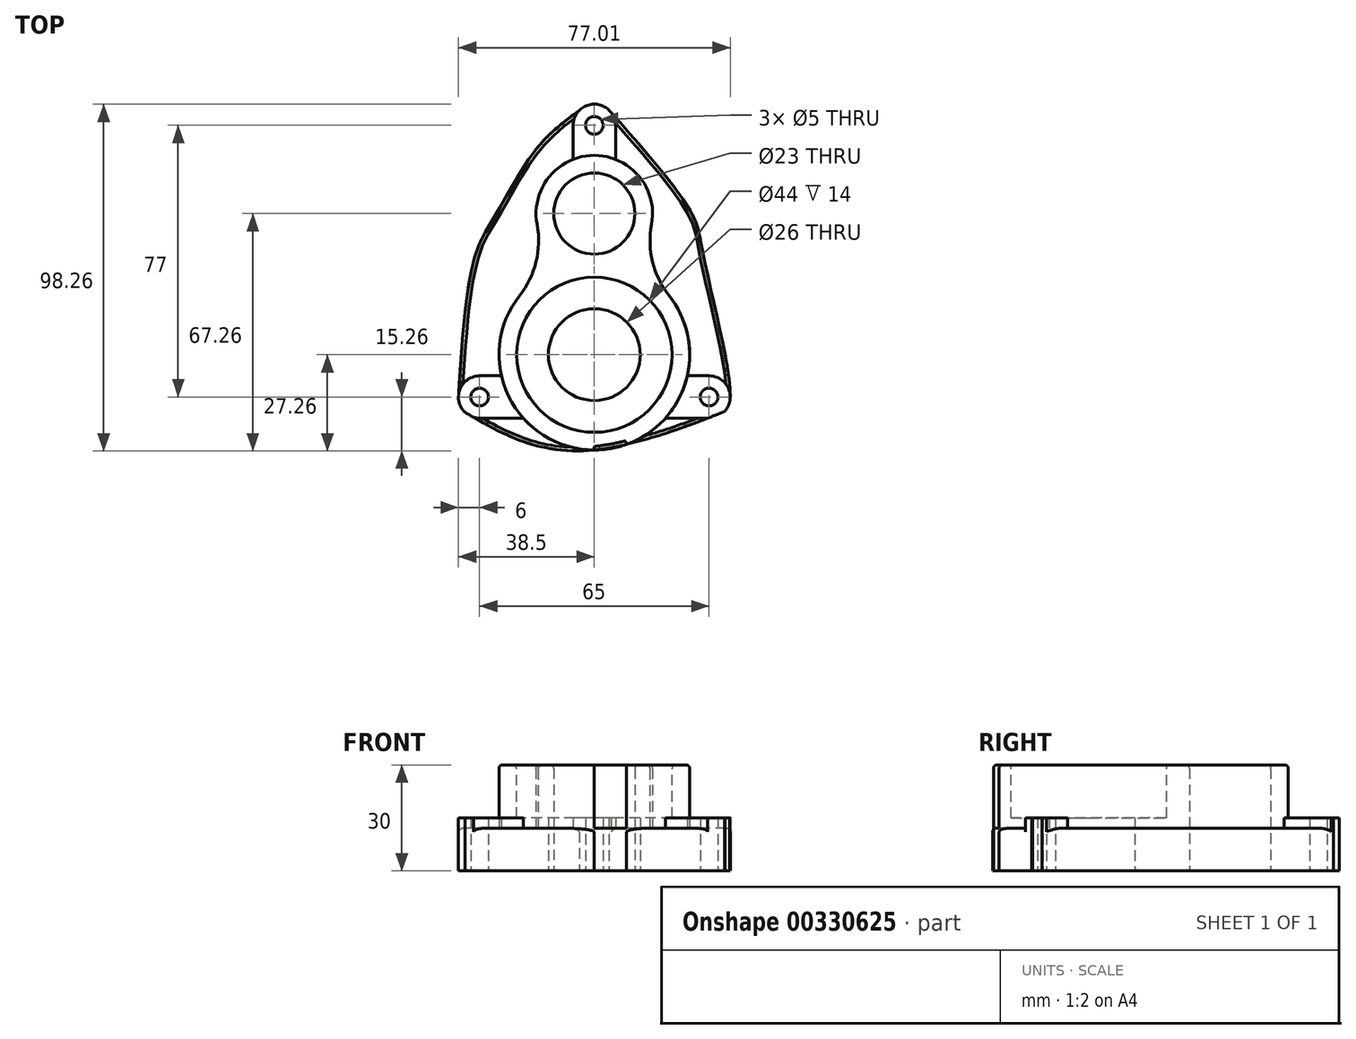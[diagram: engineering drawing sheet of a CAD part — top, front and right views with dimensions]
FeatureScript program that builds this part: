
annotation { "Feature Type Name" : "Feature", "Feature Type Description" : "" }
export const myFeature = defineFeature(function(context is Context, id is Id, definition is map)
    precondition{}
    {
        {
            var Q0;
            Q0=qCreatedBy(makeId("Top.planeOp"),FACE);
            var sketch = newSketch(context, id + "F0", { "sketchPlane" : qUnion([Q0])});
            skCircle(sketch, "E0", {"center": v(0, 0) * mm, "radius": 13 * mm});
            skCircle(sketch, "E1", {"center": v(0, 0) * mm, "radius": 22 * mm});
            skArc(sketch, "E2", {"start": v(-8.25, 25.7) * mm, "mid": v(0, -27) * mm, "end": v(8.25, 25.7) * mm});
            skCircle(sketch, "E3", {"center": v(0, 40) * mm, "radius": 11.5 * mm});
            skLineSegment(sketch, "E4", {"start": v(-46.76, -12) * mm, "end": v(88.65, -12) * mm, "construction": true});
            skLineSegment(sketch, "E5", {"start": v(85.5, 28) * mm, "end": v(-54.8, 28) * mm, "construction": true});
            skLineSegment(sketch, "E6", {"start": v(32.5, -12) * mm, "end": v(32.5, -43.46) * mm, "construction": true});
            skLineSegment(sketch, "E7", {"start": v(-32.5, -12) * mm, "end": v(-32.5, -42.32) * mm, "construction": true});
            skLineSegment(sketch, "E8", {"start": v(32.5, -43.46) * mm, "end": v(0, -43.46) * mm, "construction": true});
            skArc(sketch, "E9.0", {"start": v(8.25, 25.7) * mm, "mid": v(0, 56.5) * mm, "end": v(-8.25, 25.7) * mm});
            skCircle(sketch, "E10", {"center": v(32.5, -12) * mm, "radius": 2.5 * mm});
            skCircle(sketch, "E11", {"center": v(-32.5, -12) * mm, "radius": 2.5 * mm});
            skCircle(sketch, "E12", {"center": v(-32.5, -12) * mm, "radius": 6 * mm});
            skCircle(sketch, "E13", {"center": v(32.5, -12) * mm, "radius": 6 * mm});
            skCircle(sketch, "E14", {"center": v(0, 65) * mm, "radius": 2.5 * mm});
            skCircle(sketch, "E15", {"center": v(0, 65) * mm, "radius": 6 * mm});
            skLineSegment(sketch, "E16", {"start": v(-32.5, -6) * mm, "end": v(-26.32, -6) * mm});
            skLineSegment(sketch, "E17", {"start": v(32.5, -6) * mm, "end": v(26.32, -6) * mm});
            skLineSegment(sketch, "E18", {"start": v(32.5, -18) * mm, "end": v(20.12, -18) * mm});
            skLineSegment(sketch, "E19", {"start": v(-32.5, -18) * mm, "end": v(-20.12, -18) * mm});
            skCircle(sketch, "E20", {"center": v(-8.25, 25.7) * mm, "radius": 15 * mm, "construction": true});
            skCircle(sketch, "E21", {"center": v(8.25, 25.7) * mm, "radius": 15 * mm, "construction": true});
            skLineSegment(sketch, "E22", {"start": v(-6, 65) * mm, "end": v(-6, 55.37) * mm});
            skLineSegment(sketch, "E23", {"start": v(6, 65) * mm, "end": v(6, 55.37) * mm});
            skFitSpline(sketch, "E24", {"points": [v(-36.65, -16.33) * mm, v(0, -27) * mm, v(36.86, -16.12) * mm, v(36.84, -16.14) * mm], "startDerivative": vector(63.7, -37.15) * mm, "endDerivative": vector(-2.99, -0.84) * mm});
            skFitSpline(sketch, "E25", {"points": [v(4.21, 69.27) * mm, v(27.48, 40.3) * mm, v(30.92, 28) * mm, v(38.5, -12) * mm, v(36.86, -16.12) * mm], "startDerivative": vector(87.45, -99.48) * mm, "endDerivative": vector(-19.86, -21.82) * mm});
            skFitSpline(sketch, "E26", {"points": [v(-4.21, 69.27) * mm, v(-16.57, 58.14) * mm, v(-27.53, 40.3) * mm, v(-33.76, 28) * mm, v(-38.5, -12) * mm], "startDerivative": vector(-59.02, -43.93) * mm, "endDerivative": vector(-9.05, -137.75) * mm});
            skSolve(sketch);
        }
        {
            var Q0;
            Q0=makeQuery(id+"F0.imprint","IMPRINT",FACE,{"disambiguationData":[TD([[makeQuery(id+"F0.imprint","IMPRINT",EDGE,{"derivedFrom":sQuery(id+"F0.wireOp",EDGE,"E1")}),-1.0]])]});
            var Q1;
            {var subQ0=sQuery(id+"F0.wireOp",EDGE,"VYSbUuIq-hLQq-Rlsc-0hrW-dSPiEJNZsaO6");Q1=makeQuery(id+"F0.imprint","IMPRINT",FACE,{"disambiguationData":[TD([[makeQuery(id+"F0.imprint","IMPRINT",EDGE,{"derivedFrom":subQ0}),-1.0]])]});}
            var Q2;
            Q2=makeQuery(id+"F0.imprint","IMPRINT",FACE,{"disambiguationData":[TD([[makeQuery(id+"F0.imprint","IMPRINT",EDGE,{"derivedFrom":sQuery(id+"F0.wireOp",EDGE,"E0")}),-1.0]])]});
            var Q3;
            Q3=makeQuery(id+"F0.imprint","IMPRINT",FACE,{"disambiguationData":[TD([[makeQuery(id+"F0.imprint","IMPRINT",EDGE,{"derivedFrom":sQuery(id+"F0.wireOp",EDGE,"E0")}),1.0]])]});
            extrude(context, id + "F1", {"entities" : qUnion([Q0, Q1, Q2, Q3]), "depth" : 30 * mm});
        }
        {
            var Q0;
            {var subQ0=sQuery(id+"F0.wireOp",EDGE,"E9.0");var subQ1=sQuery(id+"F0.wireOp",EDGE,"E2");Q0=makeQuery(id+"F1.opExtrude","SWEPT_EDGE",EDGE,{"disambiguationData":[OSD([subQ1,subQ0]),TDD([makeQuery(id+"F0.imprint","INTERSECT",VERTEX,{"disambiguationData":[OD(1.0)],"derivedFrom":[subQ1,subQ0]})])]});}
            var Q1;
            {var subQ0=sQuery(id+"F0.wireOp",EDGE,"E9.0");var subQ1=sQuery(id+"F0.wireOp",EDGE,"E2");Q1=makeQuery(id+"F1.opExtrude","SWEPT_EDGE",EDGE,{"disambiguationData":[OSD([subQ1,subQ0]),TDD([makeQuery(id+"F0.imprint","INTERSECT",VERTEX,{"disambiguationData":[OD(0.0)],"derivedFrom":[subQ1,subQ0]})])]});}
            fillet(context, id + "F2", {"entities" : qUnion([Q0, Q1]), "radius" : 25 * mm, "tangentPropagation" : true, "allowEdgeOverflow" : false});
        }
        {
            var Q0;
            {var subQ0=sQuery(id+"F0.wireOp",EDGE,"E22");Q0=makeQuery(id+"F0.imprint","IMPRINT",FACE,{"disambiguationData":[TD([[makeQuery(id+"F0.imprint","IMPRINT",EDGE,{"derivedFrom":subQ0}),1.0]])]});}
            var Q1;
            Q1=makeQuery(id+"F0.imprint","IMPRINT",FACE,{"disambiguationData":[TD([[makeQuery(id+"F0.imprint","IMPRINT",EDGE,{"derivedFrom":sQuery(id+"F0.wireOp",EDGE,"E14")}),-1.0]])]});
            var Q2;
            {var subQ5=sQuery(id+"F0.wireOp",EDGE,"E17");Q2=makeQuery(id+"F0.imprint","IMPRINT",FACE,{"disambiguationData":[TD([[makeQuery(id+"F0.imprint","IMPRINT",EDGE,{"derivedFrom":subQ5}),1.0]])]});}
            var Q3;
            Q3=makeQuery(id+"F0.imprint","IMPRINT",FACE,{"disambiguationData":[TD([[makeQuery(id+"F0.imprint","IMPRINT",EDGE,{"derivedFrom":sQuery(id+"F0.wireOp",EDGE,"E10")}),-1.0]])]});
            var Q4;
            {var subQ0=sQuery(id+"F0.wireOp",EDGE,"E16");Q4=makeQuery(id+"F0.imprint","IMPRINT",FACE,{"disambiguationData":[TD([[makeQuery(id+"F0.imprint","IMPRINT",EDGE,{"derivedFrom":subQ0}),-1.0]])]});}
            var Q5;
            Q5=makeQuery(id+"F0.imprint","IMPRINT",FACE,{"disambiguationData":[TD([[makeQuery(id+"F0.imprint","IMPRINT",EDGE,{"derivedFrom":sQuery(id+"F0.wireOp",EDGE,"E11")}),-1.0]])]});
            extrude(context, id + "F3", {"entities" : qUnion([Q0, Q1, Q2, Q3, Q4, Q5]), "operationType" : NewBodyOperationType.ADD, "depth" : 15 * mm});
        }
        {
            var Q0;
            {var subQ6=sQuery(id+"F0.wireOp",EDGE,"E16");Q0=makeQuery(id+"F0.imprint","IMPRINT",FACE,{"disambiguationData":[TD([[makeQuery(id+"F0.imprint","IMPRINT",EDGE,{"derivedFrom":subQ6}),1.0]])]});}
            var Q1;
            {var subQ0=sQuery(id+"F0.wireOp",EDGE,"E17");Q1=makeQuery(id+"F0.imprint","IMPRINT",FACE,{"disambiguationData":[TD([[makeQuery(id+"F0.imprint","IMPRINT",EDGE,{"derivedFrom":subQ0}),-1.0]])]});}
            var Q2;
            {var subQ0=sQuery(id+"F0.wireOp",EDGE,"E18");var subQ1=sQuery(id+"F0.wireOp",EDGE,"E2");var subQ2=makeQuery(id+"F0.imprint","INTERSECT",VERTEX,{"derivedFrom":[subQ1,subQ0]});Q2=makeQuery(id+"F0.imprint","IMPRINT",FACE,{"disambiguationData":[TD([[makeQuery(id+"F0.imprint","IMPRINT",EDGE,{"disambiguationData":[TD([[subQ2,1.0]])],"derivedFrom":subQ1}),-1.0]])]});}
            var Q3;
            {var subQ0=sQuery(id+"F0.wireOp",EDGE,"E24");var subQ1=sQuery(id+"F0.wireOp",EDGE,"E2");var subQ2=makeQuery(id+"F0.imprint","INTERSECT",VERTEX,{"disambiguationData":[OD(0.0)],"derivedFrom":[subQ1,subQ0]});Q3=makeQuery(id+"F0.imprint","IMPRINT",FACE,{"disambiguationData":[TD([[makeQuery(id+"F0.imprint","IMPRINT",EDGE,{"disambiguationData":[TD([[subQ2,-1.0]])],"derivedFrom":subQ1}),1.0]])]});}
            var Q4;
            {var subQ0=sQuery(id+"F0.wireOp",EDGE,"E19");Q4=makeQuery(id+"F0.imprint","IMPRINT",FACE,{"disambiguationData":[TD([[makeQuery(id+"F0.imprint","IMPRINT",EDGE,{"derivedFrom":subQ0}),-1.0]])]});}
            extrude(context, id + "F4", {"entities" : qUnion([Q0, Q1, Q2, Q3, Q4]), "operationType" : NewBodyOperationType.ADD, "depth" : 12 * mm});
        }
        {
            var Q0;
            {var subQ0=sQuery(id+"F0.wireOp",EDGE,"VYSbUuIq-hLQq-Rlsc-0hrW-dSPiEJNZsaO6");Q0=makeQuery(id+"F0.imprint","IMPRINT",FACE,{"disambiguationData":[TD([[makeQuery(id+"F0.imprint","IMPRINT",EDGE,{"derivedFrom":subQ0}),-1.0]])]});}
            var Q1;
            Q1=makeQuery(id+"F0.imprint","IMPRINT",FACE,{"disambiguationData":[TD([[makeQuery(id+"F0.imprint","IMPRINT",EDGE,{"derivedFrom":sQuery(id+"F0.wireOp",EDGE,"E1")}),-1.0]])]});
            var Q2;
            Q2=makeQuery(id+"F0.imprint","IMPRINT",FACE,{"disambiguationData":[TD([[makeQuery(id+"F0.imprint","IMPRINT",EDGE,{"derivedFrom":sQuery(id+"F0.wireOp",EDGE,"E0")}),-1.0]])]});
            var Q3;
            Q3=makeQuery(id+"F0.imprint","IMPRINT",FACE,{"disambiguationData":[TD([[makeQuery(id+"F0.imprint","IMPRINT",EDGE,{"derivedFrom":sQuery(id+"F0.wireOp",EDGE,"E0")}),1.0]])]});
            extrude(context, id + "F5", {"entities" : qUnion([Q0, Q1, Q2, Q3]), "operationType" : NewBodyOperationType.ADD, "depth" : 12 * mm});
        }
        {
            var Q0;
            Q0=makeQuery(id+"F1.opExtrude","CAP_FACE",FACE,{"disambiguationData":[OSD([sQuery(id+"F0.wireOp",EDGE,"E2"),sQuery(id+"F0.wireOp",EDGE,"E3"),sQuery(id+"F0.wireOp",EDGE,"E9.0"),sQuery(id+"F0.wireOp",EDGE,"VYSbUuIq-hLQq-Rlsc-0hrW-dSPiEJNZsaO6"),sQuery(id+"F0.wireOp",EDGE,"E24")])],"isStart":false});
            var sketch = newSketch(context, id + "F6", { "sketchPlane" : qUnion([Q0])});
            skCircle(sketch, "E27.0", {"center": v(0, 0) * mm, "radius": 22 * mm});
            skSolve(sketch);
        }
        {
            var Q0;
            Q0 = qSketchRegion(id + "F6", true);
            extrude(context, id + "F7", {"entities" : qUnion([Q0]), "operationType" : NewBodyOperationType.REMOVE, "oppositeDirection" : true, "depth" : 15 * mm});
        }
        {
            var Q0;
            Q0=makeQuery(id+"F0.imprint","IMPRINT",FACE,{"disambiguationData":[TD([[makeQuery(id+"F0.imprint","IMPRINT",EDGE,{"derivedFrom":sQuery(id+"F0.wireOp",EDGE,"E0")}),1.0]])]});
            extrude(context, id + "F8", {"entities" : qUnion([Q0]), "operationType" : NewBodyOperationType.REMOVE, "endBound" : BoundingType.THROUGH_ALL, "depth" : 25 * mm});
        }
        {
            var Q0;
            Q0=makeQuery(id+"F1.opExtrude","CAP_FACE",FACE,{"disambiguationData":[OSD([sQuery(id+"F0.wireOp",EDGE,"E2"),sQuery(id+"F0.wireOp",EDGE,"E3"),sQuery(id+"F0.wireOp",EDGE,"E9.0"),sQuery(id+"F0.wireOp",EDGE,"E24")])],"isStart":false});
            var Q1;
            Q1=makeQuery(id+"F4.opExtrude","CAP_EDGE",EDGE,{"disambiguationData":[OSD([sQuery(id+"F0.wireOp",EDGE,"E25")])],"isStart":false});
            var Q2;
            {var subQ0=sQuery(id+"F0.wireOp",EDGE,"E24");Q2=makeQuery(id+"F4.opExtrude","CAP_EDGE",EDGE,{"disambiguationData":[OSD([subQ0]),TDD([makeQuery(id+"F0.imprint","IMPRINT",EDGE,{"disambiguationData":[TD([[makeQuery(id+"F0.imprint","INTERSECT",VERTEX,{"disambiguationData":[OD(1.0)],"derivedFrom":[sQuery(id+"F0.wireOp",EDGE,"E2"),subQ0]}),-1.0]])],"derivedFrom":subQ0})])],"isStart":false});}
            var Q3;
            {var subQ0=sQuery(id+"F0.wireOp",EDGE,"E24");var subQ1=sQuery(id+"F0.wireOp",EDGE,"E2");Q3=makeQuery(id+"F4.opExtrude","CAP_EDGE",EDGE,{"disambiguationData":[OSD([subQ1]),TDD([makeQuery(id+"F0.imprint","IMPRINT",EDGE,{"disambiguationData":[TD([[makeQuery(id+"F0.imprint","INTERSECT",VERTEX,{"disambiguationData":[OD(0.0)],"derivedFrom":[subQ1,subQ0]}),-1.0]])],"derivedFrom":subQ1})])],"isStart":false});}
            var Q4;
            {var subQ0=sQuery(id+"F0.wireOp",EDGE,"E24");Q4=makeQuery(id+"F4.opExtrude","CAP_EDGE",EDGE,{"disambiguationData":[OSD([subQ0]),TDD([makeQuery(id+"F0.imprint","IMPRINT",EDGE,{"disambiguationData":[TD([[makeQuery(id+"F0.imprint","INTERSECT",VERTEX,{"disambiguationData":[OD(0.0)],"derivedFrom":[sQuery(id+"F0.wireOp",EDGE,"E2"),subQ0]}),1.0]])],"derivedFrom":subQ0})])],"isStart":false});}
            var Q5;
            Q5=makeQuery(id+"F4.opExtrude","CAP_EDGE",EDGE,{"disambiguationData":[OSD([sQuery(id+"F0.wireOp",EDGE,"E26")])],"isStart":false});
            var Q6;
            {var subQ0=sQuery(id+"F0.wireOp",EDGE,"E26");Q6=makeQuery(id+"F4.boolean.opBoolean","MERGE",EDGE,{"derivedFrom":[makeQuery(id+"F3.opExtrude","CAP_EDGE",EDGE,{"disambiguationData":[OSD([subQ0])],"isStart":true}),makeQuery(id+"F4.opExtrude","CAP_EDGE",EDGE,{"disambiguationData":[OSD([subQ0])],"isStart":true})]});}
            var Q7;
            {var subQ0=sQuery(id+"F0.wireOp",EDGE,"E24");var subQ1=sQuery(id+"F0.wireOp",EDGE,"E12");Q7=makeQuery(id+"F4.boolean.opBoolean","MERGE",EDGE,{"derivedFrom":[makeQuery(id+"F3.opExtrude","CAP_EDGE",EDGE,{"disambiguationData":[OSD([subQ0]),TDD([makeQuery(id+"F0.imprint","IMPRINT",EDGE,{"disambiguationData":[TD([[makeQuery(id+"F0.imprint","INTERSECT",VERTEX,{"disambiguationData":[OD(0.0)],"derivedFrom":[subQ1,subQ0]}),-1.0]])],"derivedFrom":subQ0})])],"isStart":true}),makeQuery(id+"F4.opExtrude","CAP_EDGE",EDGE,{"disambiguationData":[OSD([subQ0]),TDD([makeQuery(id+"F0.imprint","IMPRINT",EDGE,{"disambiguationData":[TD([[makeQuery(id+"F0.imprint","INTERSECT",VERTEX,{"disambiguationData":[OD(0.0)],"derivedFrom":[sQuery(id+"F0.wireOp",EDGE,"E2"),subQ0]}),1.0]])],"derivedFrom":subQ0})])],"isStart":true})]});}
            var Q8;
            {var subQ0=sQuery(id+"F0.wireOp",EDGE,"E25");var subQ1=sQuery(id+"F0.wireOp",EDGE,"E13");var subQ2=sQuery(id+"F0.wireOp",EDGE,"E15");Q8=makeQuery(id+"F4.boolean.opBoolean","MERGE",EDGE,{"derivedFrom":[makeQuery(id+"F3.opExtrude","CAP_EDGE",EDGE,{"disambiguationData":[OSD([subQ0]),TDD([makeQuery(id+"F0.imprint","IMPRINT",EDGE,{"disambiguationData":[TD([[makeQuery(id+"F0.imprint","INTERSECT",VERTEX,{"disambiguationData":[OD(0.0)],"derivedFrom":[subQ2,subQ0]}),-1.0]])],"derivedFrom":subQ0})])],"isStart":true}),makeQuery(id+"F3.opExtrude","CAP_EDGE",EDGE,{"disambiguationData":[OSD([subQ0]),TDD([makeQuery(id+"F0.imprint","IMPRINT",EDGE,{"disambiguationData":[TD([[makeQuery(id+"F0.imprint","INTERSECT",VERTEX,{"disambiguationData":[OD(0.0)],"derivedFrom":[subQ1,subQ0]}),-1.0]])],"derivedFrom":subQ0})])],"isStart":true}),makeQuery(id+"F4.opExtrude","CAP_EDGE",EDGE,{"disambiguationData":[OSD([subQ0])],"isStart":true})]});}
            var Q9;
            {var subQ0=sQuery(id+"F0.wireOp",EDGE,"E24");var subQ1=makeQuery(id+"F0.imprint","INTERSECT",VERTEX,{"derivedFrom":[sQuery(id+"F0.wireOp",EDGE,"E18"),subQ0]});var subQ2=sQuery(id+"F0.wireOp",EDGE,"E13");var subQ3=makeQuery(id+"F0.imprint","INTERSECT",VERTEX,{"disambiguationData":[OD(1.0)],"derivedFrom":[subQ2,subQ0]});Q9=makeQuery(id+"F4.boolean.opBoolean","MERGE",EDGE,{"derivedFrom":[makeQuery(id+"F3.opExtrude","CAP_EDGE",EDGE,{"disambiguationData":[OSD([subQ0]),TDD([makeQuery(id+"F0.imprint","IMPRINT",EDGE,{"disambiguationData":[TD([[subQ1,-1.0]])],"derivedFrom":subQ0}),makeQuery(id+"F0.imprint","IMPRINT",EDGE,{"disambiguationData":[TD([[subQ3,-1.0]])],"derivedFrom":subQ0})])],"isStart":true}),makeQuery(id+"F4.opExtrude","CAP_EDGE",EDGE,{"disambiguationData":[OSD([subQ0]),TDD([makeQuery(id+"F0.imprint","IMPRINT",EDGE,{"disambiguationData":[TD([[makeQuery(id+"F0.imprint","INTERSECT",VERTEX,{"disambiguationData":[OD(1.0)],"derivedFrom":[sQuery(id+"F0.wireOp",EDGE,"E2"),subQ0]}),-1.0]])],"derivedFrom":subQ0})])],"isStart":true})]});}
            fillet(context, id + "F9", {"entities" : qUnion([Q0, Q1, Q2, Q3, Q4, Q5, Q6, Q7, Q8, Q9]), "radius" : 1 * mm, "tangentPropagation" : true, "allowEdgeOverflow" : false});
        }
    });
